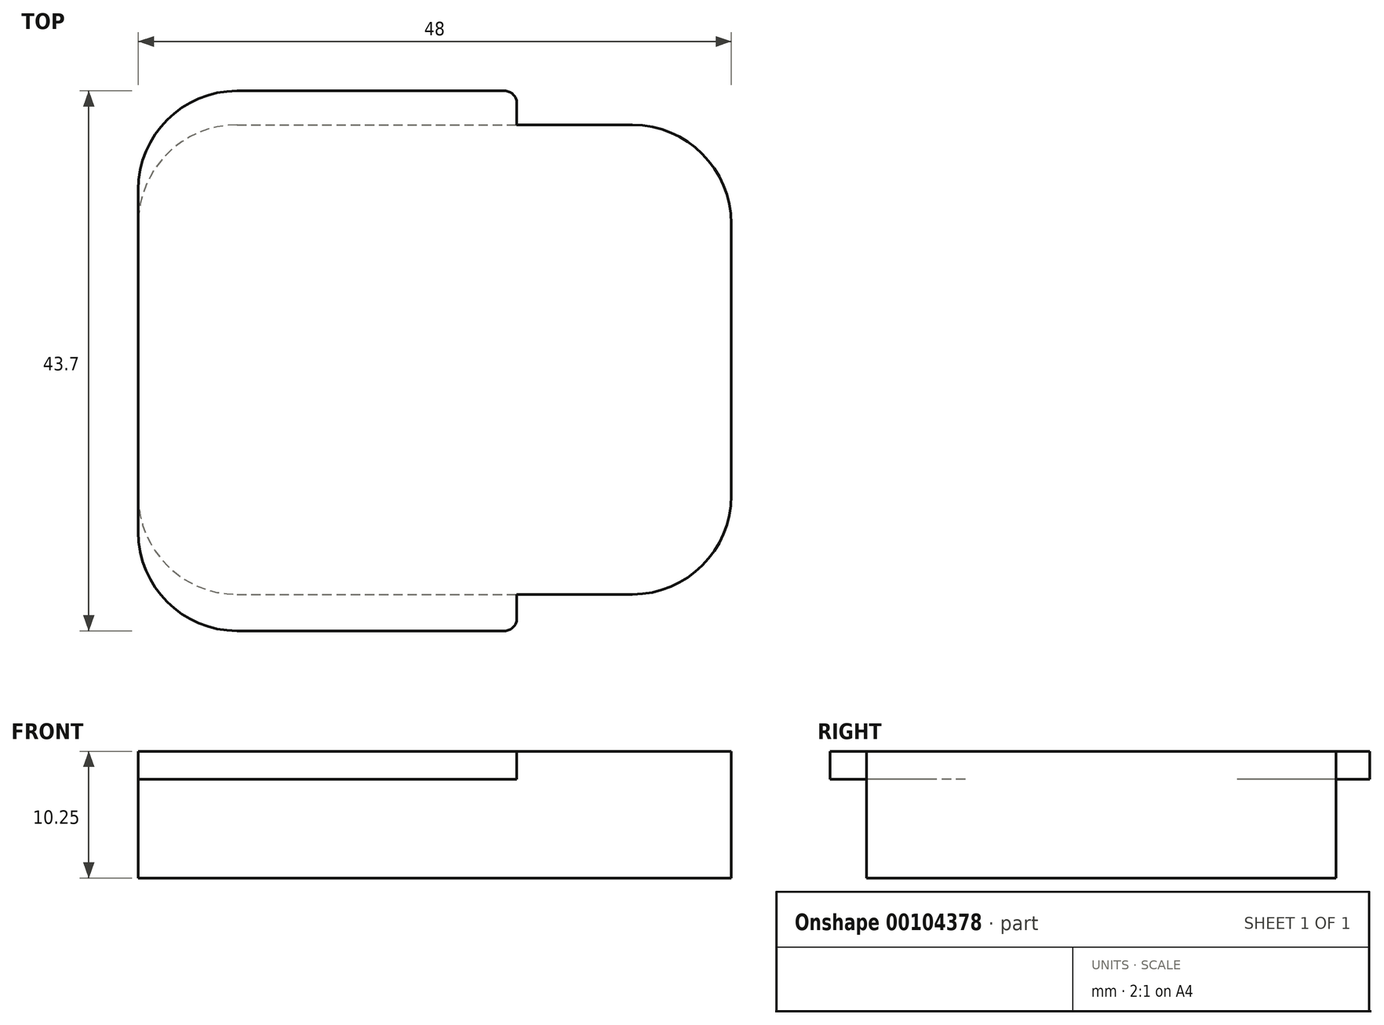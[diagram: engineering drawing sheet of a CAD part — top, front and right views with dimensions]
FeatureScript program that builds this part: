
annotation { "Feature Type Name" : "Feature", "Feature Type Description" : "" }
export const myFeature = defineFeature(function(context is Context, id is Id, definition is map)
    precondition{}
    {
        {
            var Q0;
            Q0=qCreatedBy(makeId("Top.planeOp"),FACE);
            var sketch = newSketch(context, id + "F0", { "sketchPlane" : qUnion([Q0])});
            skLineSegment(sketch, "E0.bottom", {"start": v(-16, 19) * mm, "end": v(16, 19) * mm});
            skLineSegment(sketch, "E0.top", {"start": v(-16, -19) * mm, "end": v(16, -19) * mm});
            skLineSegment(sketch, "E0.left", {"start": v(-24, 11) * mm, "end": v(-24, -11) * mm});
            skLineSegment(sketch, "E0.right", {"start": v(24, 11) * mm, "end": v(24, -11) * mm});
            skPoint(sketch, "E1.visualSharp", {"position": v(24, 19) * mm});
            skArc(sketch, "E1.filletArc", {"start": v(24, 11) * mm, "mid": v(21.66, 16.66) * mm, "end": v(16, 19) * mm});
            skPoint(sketch, "E2.visualSharp", {"position": v(24, -19) * mm});
            skArc(sketch, "E2.filletArc", {"start": v(16, -19) * mm, "mid": v(21.66, -16.66) * mm, "end": v(24, -11) * mm});
            skPoint(sketch, "E3.visualSharp", {"position": v(-24, -19) * mm});
            skArc(sketch, "E3.filletArc", {"start": v(-24, -11) * mm, "mid": v(-21.66, -16.66) * mm, "end": v(-16, -19) * mm});
            skPoint(sketch, "E4.visualSharp", {"position": v(-24, 19) * mm});
            skArc(sketch, "E4.filletArc", {"start": v(-16, 19) * mm, "mid": v(-21.66, 16.66) * mm, "end": v(-24, 11) * mm});
            skSolve(sketch);
        }
        {
            var Q0;
            Q0=makeQuery(id+"F0.imprint","IMPRINT",FACE,{"disambiguationData":[TD([[makeQuery(id+"F0.imprint","IMPRINT",EDGE,{"derivedFrom":sQuery(id+"F0.wireOp",EDGE,"E0.bottom")}),-1.0]])]});
            extrude(context, id + "F1", {"entities" : qUnion([Q0]), "depth" : 10.25 * mm});
        }
        {
            var Q0;
            Q0=makeQuery(id+"F1.opExtrude","CAP_FACE",FACE,{"disambiguationData":[OSD([sQuery(id+"F0.wireOp",EDGE,"E0.bottom"),sQuery(id+"F0.wireOp",EDGE,"E0.top"),sQuery(id+"F0.wireOp",EDGE,"E0.left"),sQuery(id+"F0.wireOp",EDGE,"E0.right"),sQuery(id+"F0.wireOp",EDGE,"E1.filletArc"),sQuery(id+"F0.wireOp",EDGE,"E2.filletArc"),sQuery(id+"F0.wireOp",EDGE,"E3.filletArc"),sQuery(id+"F0.wireOp",EDGE,"E4.filletArc")])],"isStart":false});
            var sketch = newSketch(context, id + "F2", { "sketchPlane" : qUnion([Q0])});
            skLineSegment(sketch, "E5.bottom", {"start": v(-16, 21.75) * mm, "end": v(6.65, 21.75) * mm});
            skLineSegment(sketch, "E5.top", {"start": v(-16, -21.95) * mm, "end": v(6.65, -21.95) * mm});
            skLineSegment(sketch, "E5.left", {"start": v(-24, 13.75) * mm, "end": v(-24, -13.95) * mm});
            skLineSegment(sketch, "E5.right", {"start": v(6.65, 21.75) * mm, "end": v(6.65, -21.95) * mm});
            skPoint(sketch, "E6.visualSharp", {"position": v(-24, 21.75) * mm});
            skArc(sketch, "E6.filletArc", {"start": v(-16, 21.75) * mm, "mid": v(-21.66, 19.4) * mm, "end": v(-24, 13.75) * mm});
            skPoint(sketch, "E7.visualSharp", {"position": v(-24, -21.95) * mm});
            skArc(sketch, "E7.filletArc", {"start": v(-24, -13.95) * mm, "mid": v(-21.66, -19.6) * mm, "end": v(-16, -21.95) * mm});
            skSolve(sketch);
        }
        {
            var Q0;
            {var subQ1=sQuery(id+"F2.wireOp",EDGE,"E5.top");Q0=makeQuery(id+"F2.imprint","IMPRINT",FACE,{"disambiguationData":[TD([[makeQuery(id+"F2.imprint","IMPRINT",EDGE,{"derivedFrom":subQ1}),1.0]])]});}
            var Q1;
            {var subQ1=sQuery(id+"F2.wireOp",EDGE,"E5.bottom");Q1=makeQuery(id+"F2.imprint","IMPRINT",FACE,{"disambiguationData":[TD([[makeQuery(id+"F2.imprint","IMPRINT",EDGE,{"derivedFrom":subQ1}),-1.0]])]});}
            extrude(context, id + "F3", {"entities" : qUnion([Q0, Q1]), "operationType" : NewBodyOperationType.ADD, "oppositeDirection" : true, "depth" : 2.25 * mm});
        }
        {
            var Q0;
            Q0=makeQuery(id+"F3.opExtrude","SWEPT_EDGE",EDGE,{"disambiguationData":[OSD([sQuery(id+"F2.wireOp",EDGE,"E5.bottom"),sQuery(id+"F2.wireOp",EDGE,"E5.right")])]});
            var Q1;
            Q1=makeQuery(id+"F3.opExtrude","SWEPT_EDGE",EDGE,{"disambiguationData":[OSD([sQuery(id+"F2.wireOp",EDGE,"E5.top"),sQuery(id+"F2.wireOp",EDGE,"E5.right")])]});
            var Q2;
            Q2=makeQuery(id+"F3.opExtrude","SWEPT_EDGE",EDGE,{"disambiguationData":[OSD([sQuery(id+"F0.wireOp",EDGE,"E0.top"),sQuery(id+"F2.wireOp",EDGE,"E5.right")])]});
            var Q3;
            Q3=makeQuery(id+"F3.opExtrude","SWEPT_EDGE",EDGE,{"disambiguationData":[OSD([sQuery(id+"F0.wireOp",EDGE,"E0.bottom"),sQuery(id+"F2.wireOp",EDGE,"E5.right")])]});
            fillet(context, id + "F4", {"entities" : qUnion([Q0, Q1, Q2, Q3]), "radius" : 1 * mm, "tangentPropagation" : true, "allowEdgeOverflow" : false});
        }
    });
